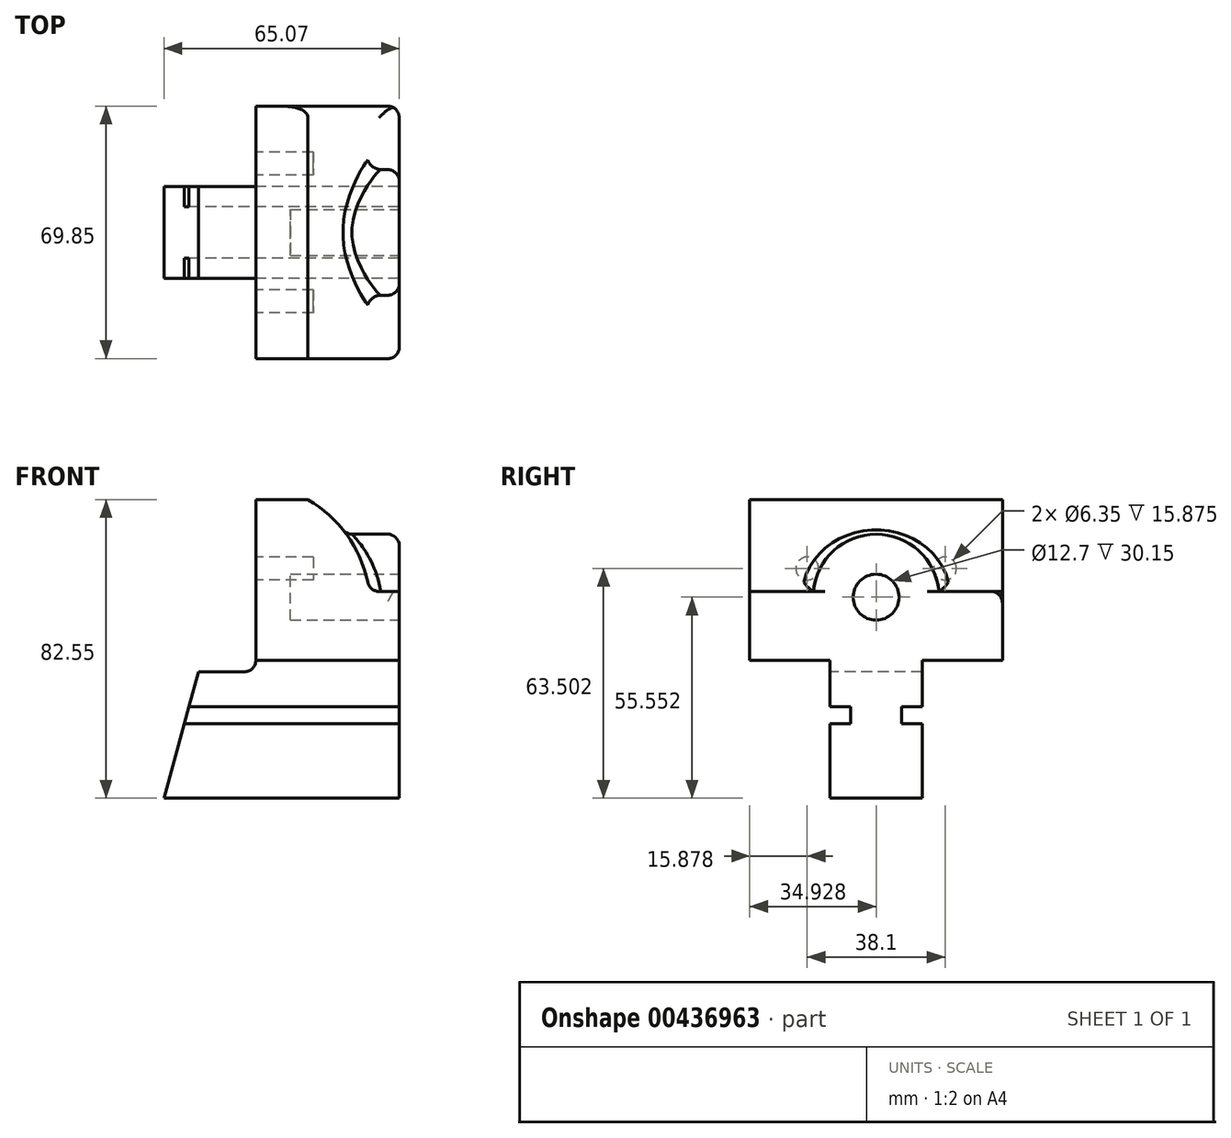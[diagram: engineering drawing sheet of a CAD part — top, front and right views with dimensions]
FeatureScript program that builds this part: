
annotation { "Feature Type Name" : "Feature", "Feature Type Description" : "" }
export const myFeature = defineFeature(function(context is Context, id is Id, definition is map)
    precondition{}
    {
        {
            var Q0;
            Q0=qCreatedBy(makeId("Right.planeOp"),FACE);
            var sketch = newSketch(context, id + "F0", { "sketchPlane" : qUnion([Q0])});
            skLineSegment(sketch, "E0.bottom", {"start": v(-37.05, 53.11) * mm, "end": v(32.8, 53.11) * mm});
            skLineSegment(sketch, "E0.top", {"start": v(-14.82, -29.44) * mm, "end": v(10.58, -29.44) * mm});
            skLineSegment(sketch, "E0.left", {"start": v(-37.05, 53.11) * mm, "end": v(-37.05, 8.66) * mm});
            skLineSegment(sketch, "E0.right", {"start": v(32.8, 53.11) * mm, "end": v(32.8, 8.66) * mm});
            skLineSegment(sketch, "E1", {"start": v(-2.12, 53.11) * mm, "end": v(-2.12, -29.44) * mm, "construction": true});
            skLineSegment(sketch, "E2", {"start": v(-37.05, 8.66) * mm, "end": v(-14.82, 8.66) * mm});
            skLineSegment(sketch, "E3", {"start": v(-14.82, 8.66) * mm, "end": v(-14.82, -4.17) * mm});
            skLineSegment(sketch, "E4.bottom", {"start": v(-14.82, -4.17) * mm, "end": v(-9.23, -4.17) * mm});
            skLineSegment(sketch, "E4.top", {"start": v(-14.82, -8.93) * mm, "end": v(-9.23, -8.93) * mm});
            skLineSegment(sketch, "E4.right", {"start": v(-9.23, -4.17) * mm, "end": v(-9.23, -8.93) * mm});
            skLineSegment(sketch, "E5.trimOffspring", {"start": v(-14.82, -8.93) * mm, "end": v(-14.82, -29.44) * mm});
            skLineSegment(sketch, "E6.MirrorCS", {"start": v(32.8, 8.66) * mm, "end": v(10.58, 8.66) * mm});
            skLineSegment(sketch, "E7.MirrorCS", {"start": v(10.58, 8.66) * mm, "end": v(10.58, -4.17) * mm});
            skLineSegment(sketch, "E8.MirrorCS", {"start": v(10.58, -4.17) * mm, "end": v(5, -4.17) * mm});
            skLineSegment(sketch, "E9.MirrorCS", {"start": v(5, -4.17) * mm, "end": v(5, -8.93) * mm});
            skLineSegment(sketch, "E10.MirrorCS", {"start": v(10.58, -8.93) * mm, "end": v(5, -8.93) * mm});
            skLineSegment(sketch, "E11.MirrorCS", {"start": v(10.58, -8.93) * mm, "end": v(10.58, -29.44) * mm});
            skPoint(sketch, "E12.orphan", {"position": v(-37.05, -29.44) * mm});
            skPoint(sketch, "E13.orphan", {"position": v(32.8, -29.44) * mm});
            skSolve(sketch);
        }
        {
            var Q0;
            Q0=qSketchRegion(id+"F0",true);
            extrude(context, id + "F1", {"entities" : qUnion([Q0]), "depth" : 65.07 * mm});
        }
        {
            var Q0;
            Q0=makeQuery(id+"F1.opExtrude","SWEPT_FACE",FACE,{"disambiguationData":[OSD([sQuery(id+"F0.wireOp",EDGE,"E0.left")])]});
            var sketch = newSketch(context, id + "F2", { "sketchPlane" : qUnion([Q0])});
            skLineSegment(sketch, "E14", {"start": v(25.4, 53.11) * mm, "end": v(25.4, 8.66) * mm});
            skArc(sketch, "E15", {"start": v(56.83, 27.71) * mm, "mid": v(51.26, 42.37) * mm, "end": v(39.85, 53.11) * mm});
            skLineSegment(sketch, "E16", {"start": v(65.07, 27.71) * mm, "end": v(25.4, 27.71) * mm});
            skLineSegment(sketch, "E17", {"start": v(65.07, 53.11) * mm, "end": v(0, 53.11) * mm});
            skLineSegment(sketch, "E18", {"start": v(0, 8.66) * mm, "end": v(0, -29.44) * mm});
            skLineSegment(sketch, "E19", {"start": v(0, -29.44) * mm, "end": v(9.52, 5.49) * mm});
            skLineSegment(sketch, "E20", {"start": v(9.53, 5.49) * mm, "end": v(22.23, 5.49) * mm});
            skPoint(sketch, "E21.newPointA", {"position": v(25.4, 5.49) * mm});
            skPoint(sketch, "E21.newPointB", {"position": v(25.4, 8.66) * mm});
            skArc(sketch, "E21.filletArc", {"start": v(22.23, 5.49) * mm, "mid": v(24.47, 6.42) * mm, "end": v(25.4, 8.66) * mm});
            skLineSegment(sketch, "E22", {"start": v(0, -29.44) * mm, "end": v(0, 53.11) * mm});
            skSolve(sketch);
        }
        {
            var Q0;
            {var subQ3=sQuery(id+"F2.wireOp",EDGE,"E19");Q0=makeQuery(id+"F2.imprint","IMPRINT",FACE,{"disambiguationData":[TD([[makeQuery(id+"F2.imprint","IMPRINT",EDGE,{"derivedFrom":subQ3}),1.0]])]});}
            var Q1;
            {var subQ1=sQuery(id+"F2.wireOp",EDGE,"E17");var subQ3=sQuery(id+"F2.wireOp",EDGE,"E14");var subQ4=makeQuery(id+"F2.imprint","INTERSECT",VERTEX,{"derivedFrom":[subQ3,subQ1]});Q1=makeQuery(id+"F2.imprint","IMPRINT",FACE,{"disambiguationData":[TD([[makeQuery(id+"F2.imprint","IMPRINT",EDGE,{"disambiguationData":[TD([[subQ4,-1.0]])],"derivedFrom":subQ3}),-1.0]])]});}
            var Q2;
            {var subQ0=sQuery(id+"F2.wireOp",EDGE,"E15");Q2=makeQuery(id+"F2.imprint","IMPRINT",FACE,{"disambiguationData":[TD([[makeQuery(id+"F2.imprint","IMPRINT",EDGE,{"derivedFrom":subQ0}),-1.0]])]});}
            extrude(context, id + "F3", {"entities" : qUnion([Q0, Q1, Q2]), "operationType" : NewBodyOperationType.REMOVE, "endBound" : BoundingType.THROUGH_ALL, "oppositeDirection" : true, "depth" : 25.4 * mm});
        }
        {
            var Q0;
            Q0=makeQuery(id+"F1.opExtrude","CAP_FACE",FACE,{"disambiguationData":[OSD([sQuery(id+"F0.wireOp",EDGE,"E0.bottom"),sQuery(id+"F0.wireOp",EDGE,"E0.top"),sQuery(id+"F0.wireOp",EDGE,"E0.left"),sQuery(id+"F0.wireOp",EDGE,"E0.right"),sQuery(id+"F0.wireOp",EDGE,"E2"),sQuery(id+"F0.wireOp",EDGE,"E3"),sQuery(id+"F0.wireOp",EDGE,"E4.bottom"),sQuery(id+"F0.wireOp",EDGE,"E4.top"),sQuery(id+"F0.wireOp",EDGE,"E4.right"),sQuery(id+"F0.wireOp",EDGE,"E5.trimOffspring"),sQuery(id+"F0.wireOp",EDGE,"E6.MirrorCS"),sQuery(id+"F0.wireOp",EDGE,"E7.MirrorCS"),sQuery(id+"F0.wireOp",EDGE,"E8.MirrorCS"),sQuery(id+"F0.wireOp",EDGE,"E9.MirrorCS"),sQuery(id+"F0.wireOp",EDGE,"E10.MirrorCS"),sQuery(id+"F0.wireOp",EDGE,"E11.MirrorCS")])],"isStart":false});
            var sketch = newSketch(context, id + "F4", { "sketchPlane" : qUnion([Q0])});
            skCircle(sketch, "E23", {"center": v(-2.12, 26.11) * mm, "radius": 17.45 * mm});
            skPoint(sketch, "E23.centerSnap0", {"position": v(-2.12, 27.71) * mm});
            skSolve(sketch);
        }
        {
            var Q0;
            Q0=qSketchRegion(id+"F4",true);
            extrude(context, id + "F5", {"entities" : qUnion([Q0]), "operationType" : NewBodyOperationType.ADD, "oppositeDirection" : true, "depth" : 25.4 * mm});
        }
        {
            var Q0;
            Q0=makeQuery(id+"F5.boolean.opBoolean","MERGE",FACE,{"derivedFrom":[makeQuery(id+"F1.opExtrude","CAP_FACE",FACE,{"disambiguationData":[OSD([sQuery(id+"F0.wireOp",EDGE,"E0.bottom"),sQuery(id+"F0.wireOp",EDGE,"E0.top"),sQuery(id+"F0.wireOp",EDGE,"E0.left"),sQuery(id+"F0.wireOp",EDGE,"E0.right"),sQuery(id+"F0.wireOp",EDGE,"E2"),sQuery(id+"F0.wireOp",EDGE,"E3"),sQuery(id+"F0.wireOp",EDGE,"E4.bottom"),sQuery(id+"F0.wireOp",EDGE,"E4.top"),sQuery(id+"F0.wireOp",EDGE,"E4.right"),sQuery(id+"F0.wireOp",EDGE,"E5.trimOffspring"),sQuery(id+"F0.wireOp",EDGE,"E6.MirrorCS"),sQuery(id+"F0.wireOp",EDGE,"E7.MirrorCS"),sQuery(id+"F0.wireOp",EDGE,"E8.MirrorCS"),sQuery(id+"F0.wireOp",EDGE,"E9.MirrorCS"),sQuery(id+"F0.wireOp",EDGE,"E10.MirrorCS"),sQuery(id+"F0.wireOp",EDGE,"E11.MirrorCS")])],"isStart":false}),makeQuery(id+"F5.opExtrude","CAP_FACE",FACE,{"disambiguationData":[OSD([sQuery(id+"F4.wireOp",EDGE,"E23")])],"isStart":true})]});
            var sketch = newSketch(context, id + "F6", { "sketchPlane" : qUnion([Q0])});
            skCircle(sketch, "E24", {"center": v(-2.12, 26.11) * mm, "radius": 6.35 * mm});
            skSolve(sketch);
        }
        {
            var Q0;
            Q0=qSketchRegion(id+"F6",true);
            extrude(context, id + "F7", {"entities" : qUnion([Q0]), "operationType" : NewBodyOperationType.REMOVE, "oppositeDirection" : true, "depth" : 30.15 * mm});
        }
        {
            var Q0;
            Q0=makeQuery(id+"F3.boolean.opBoolean","COPY",FACE,{"derivedFrom":makeQuery(id+"F3.opExtrude","SWEPT_FACE",FACE,{"disambiguationData":[OSD([sQuery(id+"F2.wireOp",EDGE,"E14")])]})});
            var sketch = newSketch(context, id + "F8", { "sketchPlane" : qUnion([Q0])});
            skLineSegment(sketch, "E25", {"start": v(-32.8, 34.06) * mm, "end": v(37.05, 34.06) * mm, "construction": true});
            skCircle(sketch, "E26", {"center": v(-16.93, 34.06) * mm, "radius": 3.18 * mm});
            skLineSegment(sketch, "E27", {"start": v(2.12, 53.11) * mm, "end": v(2.12, 8.66) * mm, "construction": true});
            skCircle(sketch, "E28.MirrorC", {"center": v(21.17, 34.06) * mm, "radius": 3.18 * mm});
            skSolve(sketch);
        }
        {
            var Q0;
            Q0=qSketchRegion(id+"F8",true);
            extrude(context, id + "F9", {"entities" : qUnion([Q0]), "operationType" : NewBodyOperationType.REMOVE, "oppositeDirection" : true, "depth" : 15.88 * mm});
        }
        {
            var Q0;
            Q0=makeQuery(id+"F3.boolean.opBoolean","COPY",EDGE,{"derivedFrom":makeQuery(id+"F3.opExtrude","CAP_EDGE",EDGE,{"disambiguationData":[OSD([sQuery(id+"F2.wireOp",EDGE,"E15")])],"isStart":true})});
            var Q1;
            Q1=makeQuery(id+"F3.boolean.opBoolean","COPY",EDGE,{"derivedFrom":makeQuery(id+"F3.opExtrude","CAP_EDGE",EDGE,{"disambiguationData":[OSD([sQuery(id+"F2.wireOp",EDGE,"E16")])],"isStart":true})});
            var Q2;
            Q2=makeQuery(id+"F1.opExtrude","CAP_EDGE",EDGE,{"disambiguationData":[OSD([sQuery(id+"F0.wireOp",EDGE,"E0.right")])],"isStart":false});
            var Q3;
            Q3=makeQuery(id+"F3.boolean.opBoolean","INTERSECT",EDGE,{"derivedFrom":[makeQuery(id+"F1.opExtrude","SWEPT_FACE",FACE,{"disambiguationData":[OSD([sQuery(id+"F0.wireOp",EDGE,"E0.right")])]}),makeQuery(id+"F3.opExtrude","SWEPT_FACE",FACE,{"disambiguationData":[OSD([sQuery(id+"F2.wireOp",EDGE,"E15")])]})]});
            var Q4;
            Q4=makeQuery(id+"F3.boolean.opBoolean","COPY",EDGE,{"derivedFrom":makeQuery(id+"F3.opExtrude","SWEPT_EDGE",EDGE,{"disambiguationData":[OSD([sQuery(id+"F2.wireOp",EDGE,"E15"),sQuery(id+"F2.wireOp",EDGE,"E17")])]})});
            var Q5;
            Q5=makeQuery(id+"F5.boolean.opBoolean","INTERSECT",EDGE,{"derivedFrom":[makeQuery(id+"F3.boolean.opBoolean","COPY",FACE,{"derivedFrom":makeQuery(id+"F3.opExtrude","SWEPT_FACE",FACE,{"disambiguationData":[OSD([sQuery(id+"F2.wireOp",EDGE,"E15")])]})}),makeQuery(id+"F5.opExtrude","SWEPT_FACE",FACE,{"disambiguationData":[OSD([sQuery(id+"F4.wireOp",EDGE,"E23")])]})]});
            var Q6;
            {var subQ0=sQuery(id+"F2.wireOp",EDGE,"E15");var subQ1=sQuery(id+"F2.wireOp",EDGE,"E16");Q6=makeQuery(id+"F5.boolean.opBoolean","SPLIT",EDGE,{"disambiguationData":[TD([makeQuery(id+"F1.opExtrude","SWEPT_FACE",FACE,{"disambiguationData":[OSD([sQuery(id+"F0.wireOp",EDGE,"E0.left")])]})])],"derivedFrom":makeQuery(id+"F3.boolean.opBoolean","COPY",EDGE,{"derivedFrom":makeQuery(id+"F3.opExtrude","SWEPT_EDGE",EDGE,{"disambiguationData":[OSD([subQ0,subQ1])]})})});}
            var Q7;
            {var subQ0=sQuery(id+"F2.wireOp",EDGE,"E15");var subQ1=sQuery(id+"F2.wireOp",EDGE,"E16");Q7=makeQuery(id+"F5.boolean.opBoolean","SPLIT",EDGE,{"disambiguationData":[TD([makeQuery(id+"F1.opExtrude","SWEPT_FACE",FACE,{"disambiguationData":[OSD([sQuery(id+"F0.wireOp",EDGE,"E0.right")])]})])],"derivedFrom":makeQuery(id+"F3.boolean.opBoolean","COPY",EDGE,{"derivedFrom":makeQuery(id+"F3.opExtrude","SWEPT_EDGE",EDGE,{"disambiguationData":[OSD([subQ0,subQ1])]})})});}
            var Q8;
            {var subQ1=sQuery(id+"F2.wireOp",EDGE,"E16");var subQ2=sQuery(id+"F0.wireOp",EDGE,"E0.left");Q8=makeQuery(id+"F5.boolean.opBoolean","SPLIT",EDGE,{"disambiguationData":[TD([makeQuery(id+"F1.opExtrude","SWEPT_FACE",FACE,{"disambiguationData":[OSD([subQ2])]})])],"derivedFrom":makeQuery(id+"F3.boolean.opBoolean","COPY",EDGE,{"derivedFrom":makeQuery(id+"F3.opExtrude","SWEPT_EDGE",EDGE,{"disambiguationData":[OSD([subQ2,subQ1])]})})});}
            var Q9;
            Q9=makeQuery(id+"F5.opExtrude","CAP_EDGE",EDGE,{"disambiguationData":[OSD([sQuery(id+"F4.wireOp",EDGE,"E23")])],"isStart":true});
            var Q10;
            {var subQ1=sQuery(id+"F2.wireOp",EDGE,"E16");var subQ2=sQuery(id+"F0.wireOp",EDGE,"E0.right");var subQ3=sQuery(id+"F0.wireOp",EDGE,"E0.left");Q10=makeQuery(id+"F5.boolean.opBoolean","SPLIT",EDGE,{"disambiguationData":[TD([makeQuery(id+"F1.opExtrude","SWEPT_FACE",FACE,{"disambiguationData":[OSD([subQ2])]})])],"derivedFrom":makeQuery(id+"F3.boolean.opBoolean","COPY",EDGE,{"derivedFrom":makeQuery(id+"F3.opExtrude","SWEPT_EDGE",EDGE,{"disambiguationData":[OSD([subQ3,subQ1])]})})});}
            var Q11;
            Q11=makeQuery(id+"F1.opExtrude","CAP_EDGE",EDGE,{"disambiguationData":[OSD([sQuery(id+"F0.wireOp",EDGE,"E0.left")])],"isStart":false});
            fillet(context, id + "F10", {"entities" : qUnion([Q0, Q1, Q2, Q3, Q4, Q5, Q6, Q7, Q8, Q9, Q10, Q11]), "radius" : 3.17 * mm, "tangentPropagation" : true, "allowEdgeOverflow" : false});
        }
    });
